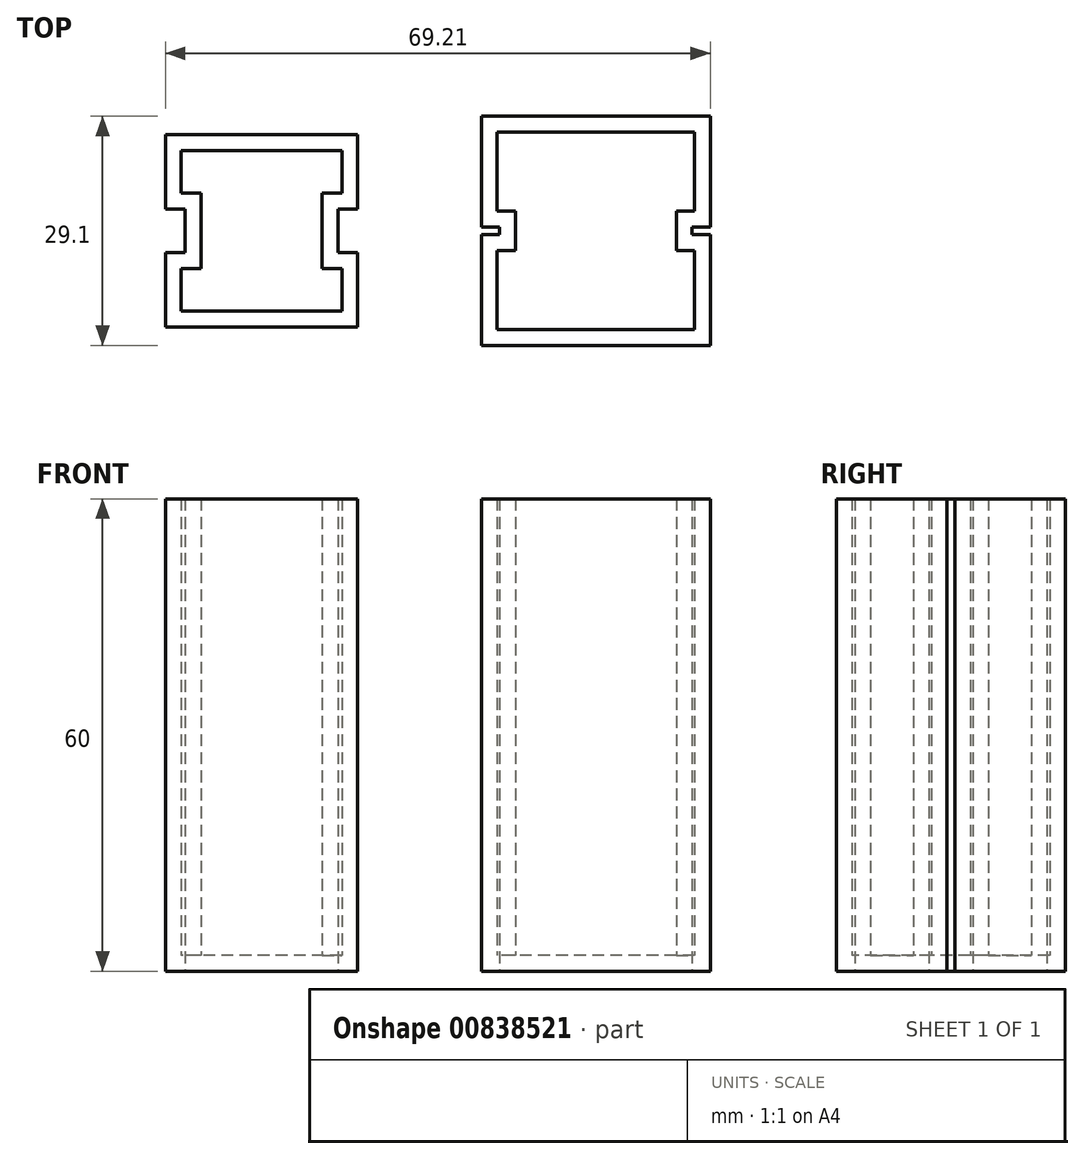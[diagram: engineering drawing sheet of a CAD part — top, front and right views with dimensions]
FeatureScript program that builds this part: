
annotation { "Feature Type Name" : "Feature", "Feature Type Description" : "" }
export const myFeature = defineFeature(function(context is Context, id is Id, definition is map)
    precondition{}
    {
        {
            var Q0;
            Q0=qCreatedBy(makeId("Top.planeOp"),FACE);
            var sketch = newSketch(context, id + "F0", { "sketchPlane" : qUnion([Q0])});
            skLineSegment(sketch, "E0.bottom", {"start": v(12.2, -12.2) * mm, "end": v(-12.2, -12.2) * mm});
            skLineSegment(sketch, "E0.top", {"start": v(12.2, 12.2) * mm, "end": v(-12.2, 12.2) * mm});
            skLineSegment(sketch, "E0.left", {"start": v(12.2, -12.2) * mm, "end": v(12.2, -2.77) * mm});
            skLineSegment(sketch, "E0.right", {"start": v(-12.2, -12.2) * mm, "end": v(-12.2, -2.77) * mm});
            skPoint(sketch, "E0.middle", {"position": v(0, 0) * mm});
            skLineSegment(sketch, "E1.bottom", {"start": v(9.7, 2.77) * mm, "end": v(12.2, 2.77) * mm});
            skLineSegment(sketch, "E1.top", {"start": v(9.7, -2.77) * mm, "end": v(12.2, -2.77) * mm});
            skLineSegment(sketch, "E1.left", {"start": v(9.7, 2.77) * mm, "end": v(9.7, -2.77) * mm});
            skPoint(sketch, "E1.middle", {"position": v(12.2, 0) * mm});
            skLineSegment(sketch, "E2", {"start": v(0, 12.2) * mm, "end": v(0, -12.2) * mm, "construction": true});
            skLineSegment(sketch, "E3.MirrorCS", {"start": v(-9.7, 2.77) * mm, "end": v(-9.7, -2.77) * mm});
            skLineSegment(sketch, "E4.MirrorCS", {"start": v(-9.7, -2.77) * mm, "end": v(-12.2, -2.77) * mm});
            skLineSegment(sketch, "E5.MirrorCS", {"start": v(-9.7, 2.77) * mm, "end": v(-12.2, 2.77) * mm});
            skLineSegment(sketch, "E6.trimOffspring", {"start": v(-12.2, 2.77) * mm, "end": v(-12.2, 12.2) * mm});
            skPoint(sketch, "E7.orphan", {"position": v(-14.7, 2.77) * mm});
            skPoint(sketch, "E8.orphan", {"position": v(-14.7, -2.77) * mm});
            skPoint(sketch, "E9.orphan", {"position": v(14.7, -2.77) * mm});
            skLineSegment(sketch, "E10.trimOffspring", {"start": v(12.2, 2.77) * mm, "end": v(12.2, 12.2) * mm});
            skPoint(sketch, "E11.orphan", {"position": v(14.7, 2.77) * mm});
            skLineSegment(sketch, "E12.bottom", {"start": v(57, 14.55) * mm, "end": v(27.9, 14.55) * mm});
            skLineSegment(sketch, "E12.top", {"start": v(57, -14.55) * mm, "end": v(27.9, -14.55) * mm});
            skLineSegment(sketch, "E12.left", {"start": v(57, 14.55) * mm, "end": v(57, 0.5) * mm});
            skLineSegment(sketch, "E12.right", {"start": v(27.9, 14.55) * mm, "end": v(27.9, 0.5) * mm});
            skPoint(sketch, "E12.middle", {"position": v(42.46, 0) * mm});
            skLineSegment(sketch, "E13.bottom", {"start": v(30.23, 0.5) * mm, "end": v(27.9, 0.5) * mm});
            skLineSegment(sketch, "E13.top", {"start": v(30.23, -0.5) * mm, "end": v(27.9, -0.5) * mm});
            skLineSegment(sketch, "E13.left", {"start": v(30.23, 0.5) * mm, "end": v(30.23, -0.5) * mm});
            skPoint(sketch, "E13.middle", {"position": v(27.9, 0) * mm});
            skLineSegment(sketch, "E14", {"start": v(42.46, 14.55) * mm, "end": v(42.46, -14.55) * mm, "construction": true});
            skLineSegment(sketch, "E15.MirrorCS", {"start": v(54.69, -0.5) * mm, "end": v(57, -0.5) * mm});
            skLineSegment(sketch, "E16.MirrorCS", {"start": v(54.69, 0.5) * mm, "end": v(57, 0.5) * mm});
            skLineSegment(sketch, "E17.MirrorCS", {"start": v(54.69, 0.5) * mm, "end": v(54.69, -0.5) * mm});
            skLineSegment(sketch, "E18.trimOffspring", {"start": v(57, -0.5) * mm, "end": v(57, -14.55) * mm});
            skPoint(sketch, "E19.orphan", {"position": v(59.33, 0.5) * mm});
            skPoint(sketch, "E20.orphan", {"position": v(59.33, -0.5) * mm});
            skPoint(sketch, "E21.orphan", {"position": v(25.59, 0.5) * mm});
            skPoint(sketch, "E22.orphan", {"position": v(25.59, -0.5) * mm});
            skLineSegment(sketch, "E23.trimOffspring", {"start": v(27.9, -0.5) * mm, "end": v(27.9, -14.55) * mm});
            skSolve(sketch);
        }
        {
            var Q0;
            Q0=makeQuery(id+"F0.imprint","IMPRINT",FACE,{"disambiguationData":[TD([[makeQuery(id+"F0.imprint","IMPRINT",EDGE,{"derivedFrom":sQuery(id+"F0.wireOp",EDGE,"E0.bottom")}),-1.0]])]});
            var Q1;
            Q1=makeQuery(id+"F0.imprint","IMPRINT",FACE,{"disambiguationData":[TD([[makeQuery(id+"F0.imprint","IMPRINT",EDGE,{"derivedFrom":sQuery(id+"F0.wireOp",EDGE,"E12.bottom")}),1.0]])]});
            extrude(context, id + "F1", {"entities" : qUnion([Q0, Q1]), "depth" : 60 * mm, "offsetDistance" : 25 * mm});
        }
        {
            var Q0;
            Q0=makeQuery(id+"F1.opExtrude","CAP_FACE",FACE,{"disambiguationData":[OSD([sQuery(id+"F0.wireOp",EDGE,"E0.bottom"),sQuery(id+"F0.wireOp",EDGE,"E0.top"),sQuery(id+"F0.wireOp",EDGE,"E0.left"),sQuery(id+"F0.wireOp",EDGE,"E0.right")])],"isStart":false});
            var Q1;
            Q1=makeQuery(id+"F1.opExtrude","CAP_FACE",FACE,{"disambiguationData":[OSD([sQuery(id+"F0.wireOp",EDGE,"E12.bottom"),sQuery(id+"F0.wireOp",EDGE,"E12.top"),sQuery(id+"F0.wireOp",EDGE,"E12.left"),sQuery(id+"F0.wireOp",EDGE,"E12.right"),sQuery(id+"F0.wireOp",EDGE,"E13.bottom"),sQuery(id+"F0.wireOp",EDGE,"E13.top"),sQuery(id+"F0.wireOp",EDGE,"E13.left"),sQuery(id+"F0.wireOp",EDGE,"E15.MirrorCS"),sQuery(id+"F0.wireOp",EDGE,"E16.MirrorCS"),sQuery(id+"F0.wireOp",EDGE,"E17.MirrorCS"),sQuery(id+"F0.wireOp",EDGE,"E18.trimOffspring"),sQuery(id+"F0.wireOp",EDGE,"E23.trimOffspring")])],"isStart":false});
            shell(context, id + "F2", {"entities" : qUnion([Q0, Q1]), "thickness" : 2 * mm});
        }
    });
